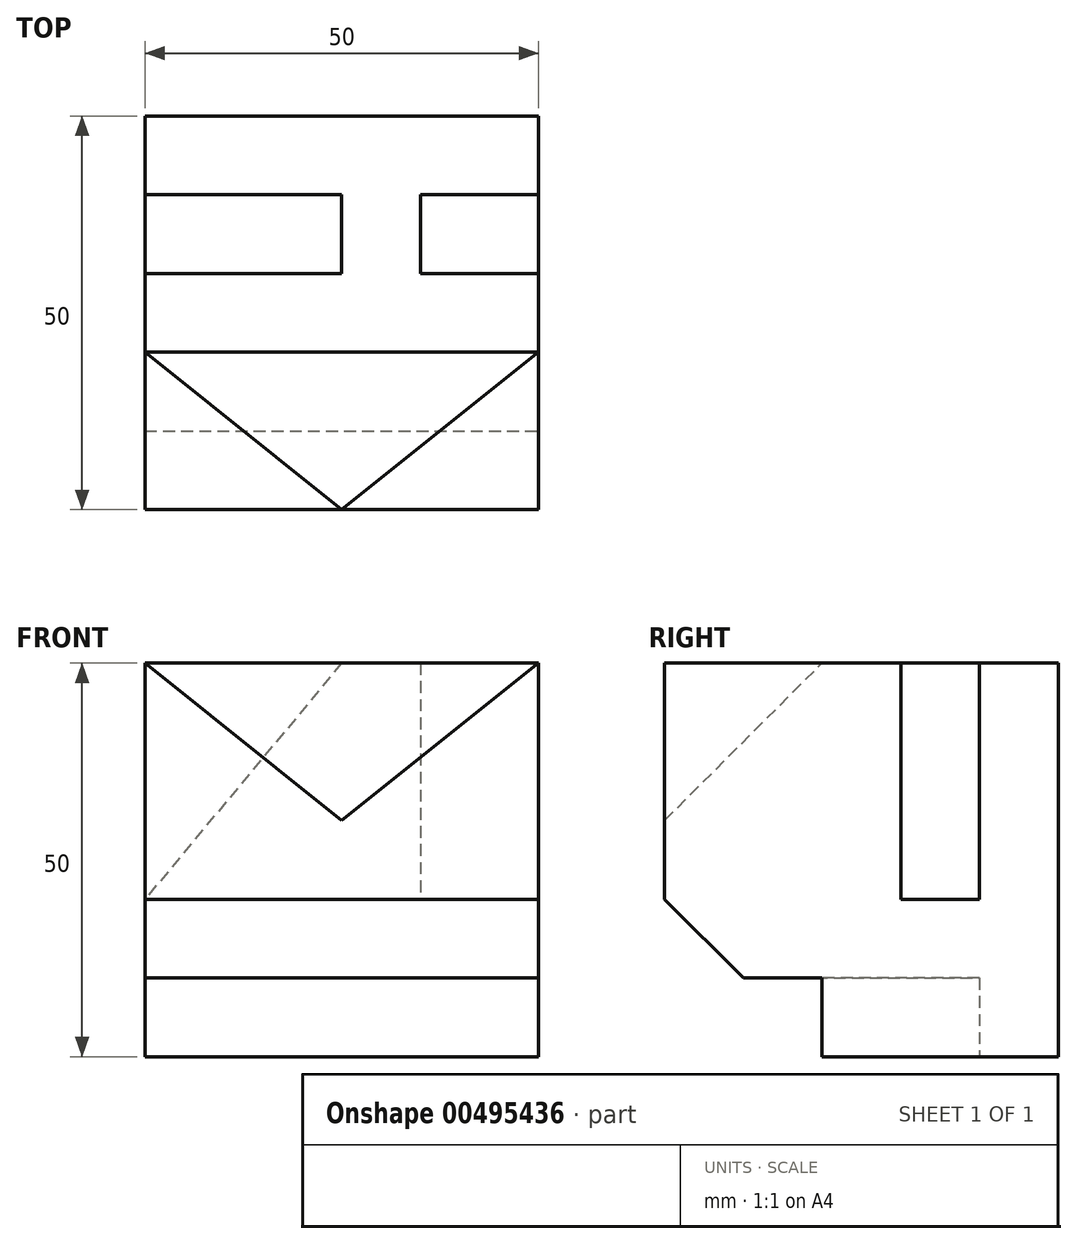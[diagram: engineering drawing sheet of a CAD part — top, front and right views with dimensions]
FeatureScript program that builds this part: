
annotation { "Feature Type Name" : "Feature", "Feature Type Description" : "" }
export const myFeature = defineFeature(function(context is Context, id is Id, definition is map)
    precondition{}
    {
        {
            var Q0;
            Q0=qCreatedBy(makeId("Front.planeOp"),FACE);
            var sketch = newSketch(context, id + "F0", { "sketchPlane" : qUnion([Q0])});
            skLineSegment(sketch, "E0.bottom", {"start": v(-38.9, -30.63) * mm, "end": v(11.1, -30.63) * mm});
            skLineSegment(sketch, "E0.top", {"start": v(-38.9, 19.37) * mm, "end": v(11.1, 19.37) * mm});
            skLineSegment(sketch, "E0.left", {"start": v(-38.9, -30.63) * mm, "end": v(-38.9, 19.37) * mm});
            skLineSegment(sketch, "E0.right", {"start": v(11.1, -30.63) * mm, "end": v(11.1, 19.37) * mm});
            skSolve(sketch);
        }
        {
            var Q0;
            Q0=makeQuery(id+"F0.imprint","IMPRINT",FACE,{"disambiguationData":[TD([[makeQuery(id+"F0.imprint","IMPRINT",EDGE,{"derivedFrom":sQuery(id+"F0.wireOp",EDGE,"E0.bottom")}),1.0]])]});
            extrude(context, id + "F1", {"entities" : qUnion([Q0]), "depth" : 50 * mm});
        }
        {
            var Q0;
            Q0=makeQuery(id+"F1.opExtrude","SWEPT_FACE",FACE,{"disambiguationData":[OSD([sQuery(id+"F0.wireOp",EDGE,"E0.right")])]});
            var sketch = newSketch(context, id + "F2", { "sketchPlane" : qUnion([Q0])});
            skLineSegment(sketch, "E1.bottom", {"start": v(-50, -30.63) * mm, "end": v(-30, -30.63) * mm});
            skLineSegment(sketch, "E1.top", {"start": v(-50, -20.63) * mm, "end": v(-30, -20.63) * mm});
            skLineSegment(sketch, "E1.left", {"start": v(-50, -30.63) * mm, "end": v(-50, -20.63) * mm});
            skLineSegment(sketch, "E1.right", {"start": v(-30, -30.63) * mm, "end": v(-30, -20.63) * mm});
            skLineSegment(sketch, "E2", {"start": v(-50, -20.63) * mm, "end": v(-50, -10.63) * mm});
            skLineSegment(sketch, "E3", {"start": v(-50, -10.63) * mm, "end": v(-40, -20.63) * mm});
            skLineSegment(sketch, "E4", {"start": v(-40, -20.63) * mm, "end": v(-50, -20.63) * mm});
            skLineSegment(sketch, "E5", {"start": v(0, 19.37) * mm, "end": v(-10, 19.37) * mm});
            skLineSegment(sketch, "E6.bottom", {"start": v(-10, 19.37) * mm, "end": v(-20, 19.37) * mm});
            skLineSegment(sketch, "E6.top", {"start": v(-10, -10.63) * mm, "end": v(-20, -10.63) * mm});
            skLineSegment(sketch, "E6.left", {"start": v(-10, 19.37) * mm, "end": v(-10, -10.63) * mm});
            skLineSegment(sketch, "E6.right", {"start": v(-20, 19.37) * mm, "end": v(-20, -10.63) * mm});
            skSolve(sketch);
        }
        {
            var Q0;
            Q0=makeQuery(id+"F2.imprint","IMPRINT",FACE,{"disambiguationData":[TD([[makeQuery(id+"F2.imprint","IMPRINT",EDGE,{"derivedFrom":sQuery(id+"F2.wireOp",EDGE,"E6.bottom")}),-1.0]])]});
            extrude(context, id + "F3", {"entities" : qUnion([Q0]), "operationType" : NewBodyOperationType.REMOVE, "oppositeDirection" : true, "depth" : 15 * mm});
        }
        {
            var Q0;
            Q0=makeQuery(id+"F2.imprint","IMPRINT",FACE,{"disambiguationData":[TD([[makeQuery(id+"F2.imprint","IMPRINT",EDGE,{"derivedFrom":sQuery(id+"F2.wireOp",EDGE,"E2")}),-1.0]])]});
            extrude(context, id + "F4", {"entities" : qUnion([Q0]), "operationType" : NewBodyOperationType.REMOVE, "oppositeDirection" : true, "depth" : 50 * mm});
        }
        {
            var Q0;
            Q0=makeQuery(id+"F2.imprint","IMPRINT",FACE,{"disambiguationData":[TD([[makeQuery(id+"F2.imprint","IMPRINT",EDGE,{"derivedFrom":sQuery(id+"F2.wireOp",EDGE,"E1.bottom")}),1.0]])]});
            extrude(context, id + "F5", {"entities" : qUnion([Q0]), "operationType" : NewBodyOperationType.REMOVE, "oppositeDirection" : true, "depth" : 50 * mm});
        }
        {
            var Q0;
            {var subQ0=sQuery(id+"F0.wireOp",EDGE,"E0.top");var subQ1=sQuery(id+"F0.wireOp",EDGE,"E0.left");var subQ2=sQuery(id+"F0.wireOp",EDGE,"E0.right");Q0=makeQuery(id+"F4.boolean.opBoolean","SPLIT",FACE,{"disambiguationData":[TD([makeQuery(id+"F1.opExtrude","SWEPT_FACE",FACE,{"disambiguationData":[OSD([subQ0])]})])],"derivedFrom":makeQuery(id+"F1.opExtrude","CAP_FACE",FACE,{"disambiguationData":[OSD([sQuery(id+"F0.wireOp",EDGE,"E0.bottom"),subQ0,subQ1,subQ2])],"isStart":false})});}
            var sketch = newSketch(context, id + "F6", { "sketchPlane" : qUnion([Q0])});
            skLineSegment(sketch, "E7", {"start": v(-38.9, 19.37) * mm, "end": v(-13.9, 19.37) * mm});
            skLineSegment(sketch, "E8", {"start": v(-13.9, 19.37) * mm, "end": v(-13.9, -0.63) * mm});
            skLineSegment(sketch, "E9", {"start": v(-13.9, -0.63) * mm, "end": v(-38.9, 19.37) * mm});
            skLineSegment(sketch, "E10", {"start": v(-13.9, -0.63) * mm, "end": v(11.1, 19.37) * mm});
            skLineSegment(sketch, "E11", {"start": v(11.1, 19.37) * mm, "end": v(-13.9, 19.37) * mm});
            skSolve(sketch);
        }
        {
            var Q0;
            Q0=makeQuery(id+"F1.opExtrude","SWEPT_FACE",FACE,{"disambiguationData":[OSD([sQuery(id+"F0.wireOp",EDGE,"E0.top")])]});
            var sketch = newSketch(context, id + "F7", { "sketchPlane" : qUnion([Q0])});
            skLineSegment(sketch, "E12", {"start": v(-13.9, -50) * mm, "end": v(-13.9, -30) * mm});
            skLineSegment(sketch, "E13", {"start": v(-13.9, -30) * mm, "end": v(-38.9, -30) * mm});
            skLineSegment(sketch, "E14", {"start": v(-38.9, -30) * mm, "end": v(-13.9, -50) * mm});
            skLineSegment(sketch, "E15", {"start": v(-13.9, -30) * mm, "end": v(11.1, -30) * mm});
            skLineSegment(sketch, "E16", {"start": v(11.1, -30) * mm, "end": v(-13.9, -50) * mm});
            skSolve(sketch);
        }
        {
            var Q0;
            Q0=sQuery(id+"F6.wireOp",VERTEX,"E9.end");
            var Q1;
            Q1=sQuery(id+"F7.wireOp",VERTEX,"E14.start");
            var Q2;
            Q2=sQuery(id+"F6.wireOp",VERTEX,"E10.start");
            cPlane(context, id + "F8", {"entities" : qUnion([Q0, Q1, Q2]), "cplaneType" : CPlaneType.THREE_POINT, "offset" : 25 * mm, "width" : 150 * mm, "height" : 150 * mm});
        }
        {
            var Q0;
            {var subQ0=sQuery(id+"F7.wireOp",EDGE,"E14");Q0=makeQuery(id+"F7.imprint","IMPRINT",FACE,{"disambiguationData":[TD([[makeQuery(id+"F7.imprint","IMPRINT",EDGE,{"derivedFrom":subQ0}),-1.0]])]});}
            var Q1;
            Q1=qCreatedBy(id+"F8.planeOp",FACE);
            extrude(context, id + "F9", {"entities" : qUnion([Q0]), "operationType" : NewBodyOperationType.REMOVE, "endBound" : BoundingType.UP_TO_SURFACE, "oppositeDirection" : true, "endBoundEntityFace" : qUnion([Q1]), "depth" : 25 * mm});
        }
        {
            var Q0;
            Q0=sQuery(id+"F6.wireOp",VERTEX,"E10.start");
            var Q1;
            Q1=sQuery(id+"F6.wireOp",VERTEX,"E10.end");
            var Q2;
            Q2=sQuery(id+"F7.wireOp",VERTEX,"E16.start");
            cPlane(context, id + "F10", {"entities" : qUnion([Q0, Q1, Q2]), "cplaneType" : CPlaneType.THREE_POINT, "offset" : 25 * mm, "width" : 150 * mm, "height" : 150 * mm});
        }
        {
            var Q0;
            {var subQ0=sQuery(id+"F7.wireOp",EDGE,"E16");Q0=makeQuery(id+"F7.imprint","IMPRINT",FACE,{"disambiguationData":[TD([[makeQuery(id+"F7.imprint","IMPRINT",EDGE,{"derivedFrom":subQ0}),1.0]])]});}
            var Q1;
            Q1=qCreatedBy(id+"F10.planeOp",FACE);
            extrude(context, id + "F11", {"entities" : qUnion([Q0]), "operationType" : NewBodyOperationType.REMOVE, "endBound" : BoundingType.UP_TO_SURFACE, "oppositeDirection" : true, "endBoundEntityFace" : qUnion([Q1]), "depth" : 25 * mm});
        }
        {
            var Q0;
            Q0=sQuery(id+"F7.wireOp",VERTEX,"E14.start");
            var Q1;
            Q1=sQuery(id+"F7.wireOp",VERTEX,"E16.start");
            var Q2;
            Q2=sQuery(id+"F6.wireOp",VERTEX,"E10.start");
            cPlane(context, id + "F12", {"entities" : qUnion([Q0, Q1, Q2]), "cplaneType" : CPlaneType.THREE_POINT, "offset" : 25 * mm, "width" : 150 * mm, "height" : 150 * mm});
        }
        {
            var Q0;
            Q0=makeQuery(id+"F7.imprint","IMPRINT",FACE,{"disambiguationData":[TD([[makeQuery(id+"F7.imprint","IMPRINT",EDGE,{"derivedFrom":sQuery(id+"F7.wireOp",EDGE,"E12")}),1.0]])]});
            var Q1;
            Q1=makeQuery(id+"F7.imprint","IMPRINT",FACE,{"disambiguationData":[TD([[makeQuery(id+"F7.imprint","IMPRINT",EDGE,{"derivedFrom":sQuery(id+"F7.wireOp",EDGE,"E12")}),-1.0]])]});
            var Q2;
            Q2=qCreatedBy(id+"F12.planeOp",FACE);
            extrude(context, id + "F13", {"entities" : qUnion([Q0, Q1]), "operationType" : NewBodyOperationType.REMOVE, "endBound" : BoundingType.UP_TO_SURFACE, "oppositeDirection" : true, "endBoundEntityFace" : qUnion([Q2]), "depth" : 25 * mm});
        }
        {
            var Q0;
            Q0=makeQuery(id+"F1.opExtrude","SWEPT_FACE",FACE,{"disambiguationData":[OSD([sQuery(id+"F0.wireOp",EDGE,"E0.left")])]});
            var sketch = newSketch(context, id + "F14", { "sketchPlane" : qUnion([Q0])});
            skLineSegment(sketch, "E17", {"start": v(0, 19.37) * mm, "end": v(10, 19.37) * mm});
            skLineSegment(sketch, "E18.bottom", {"start": v(10, 19.37) * mm, "end": v(20, 19.37) * mm});
            skLineSegment(sketch, "E18.top", {"start": v(10, -10.63) * mm, "end": v(20, -10.63) * mm});
            skLineSegment(sketch, "E18.left", {"start": v(10, 19.37) * mm, "end": v(10, -10.63) * mm});
            skLineSegment(sketch, "E18.right", {"start": v(20, 19.37) * mm, "end": v(20, -10.63) * mm});
            skSolve(sketch);
        }
        {
            var Q0;
            Q0=makeQuery(id+"F1.opExtrude","SWEPT_FACE",FACE,{"disambiguationData":[OSD([sQuery(id+"F0.wireOp",EDGE,"E0.top")])]});
            var sketch = newSketch(context, id + "F15", { "sketchPlane" : qUnion([Q0])});
            skLineSegment(sketch, "E19", {"start": v(-38.9, 0) * mm, "end": v(-38.9, -10) * mm});
            skLineSegment(sketch, "E20.bottom", {"start": v(-38.9, -10) * mm, "end": v(-13.9, -10) * mm});
            skLineSegment(sketch, "E20.top", {"start": v(-38.9, -20) * mm, "end": v(-13.9, -20) * mm});
            skLineSegment(sketch, "E20.left", {"start": v(-38.9, -10) * mm, "end": v(-38.9, -20) * mm});
            skLineSegment(sketch, "E20.right", {"start": v(-13.9, -10) * mm, "end": v(-13.9, -20) * mm});
            skSolve(sketch);
        }
        {
            var Q0;
            Q0=sQuery(id+"F15.wireOp",VERTEX,"E20.bottom.end");
            var Q1;
            Q1=sQuery(id+"F15.wireOp",VERTEX,"E20.top.end");
            var Q2;
            Q2=sQuery(id+"F14.wireOp",VERTEX,"E18.top.end");
            cPlane(context, id + "F16", {"entities" : qUnion([Q0, Q1, Q2]), "cplaneType" : CPlaneType.THREE_POINT, "offset" : 25 * mm, "width" : 150 * mm, "height" : 150 * mm});
        }
        {
            var Q0;
            Q0=makeQuery(id+"F15.imprint","IMPRINT",FACE,{"disambiguationData":[TD([[makeQuery(id+"F15.imprint","IMPRINT",EDGE,{"derivedFrom":sQuery(id+"F15.wireOp",EDGE,"E20.bottom")}),-1.0]])]});
            var Q1;
            Q1=qCreatedBy(id+"F16.planeOp",FACE);
            extrude(context, id + "F17", {"entities" : qUnion([Q0]), "operationType" : NewBodyOperationType.REMOVE, "endBound" : BoundingType.UP_TO_SURFACE, "oppositeDirection" : true, "endBoundEntityFace" : qUnion([Q1]), "depth" : 25 * mm});
        }
        {
            var Q0;
            Q0=makeQuery(id+"F1.opExtrude","SWEPT_FACE",FACE,{"disambiguationData":[OSD([sQuery(id+"F0.wireOp",EDGE,"E0.bottom")])]});
            var sketch = newSketch(context, id + "F18", { "sketchPlane" : qUnion([Q0])});
            skLineSegment(sketch, "E21", {"start": v(-38.9, 0) * mm, "end": v(-38.9, 10) * mm});
            skLineSegment(sketch, "E22", {"start": v(-38.9, 10) * mm, "end": v(11.1, 30) * mm});
            skLineSegment(sketch, "E23", {"start": v(-38.9, 10) * mm, "end": v(-38.9, 30) * mm});
            skLineSegment(sketch, "E24", {"start": v(-38.9, 30) * mm, "end": v(11.1, 30) * mm});
            skSolve(sketch);
        }
        {
            var Q0;
            Q0=makeQuery(id+"F18.imprint","IMPRINT",FACE,{"disambiguationData":[TD([[makeQuery(id+"F18.imprint","IMPRINT",EDGE,{"derivedFrom":sQuery(id+"F18.wireOp",EDGE,"E22")}),1.0]])]});
            extrude(context, id + "F19", {"entities" : qUnion([Q0]), "operationType" : NewBodyOperationType.REMOVE, "oppositeDirection" : true, "depth" : 10 * mm});
        }
    });
